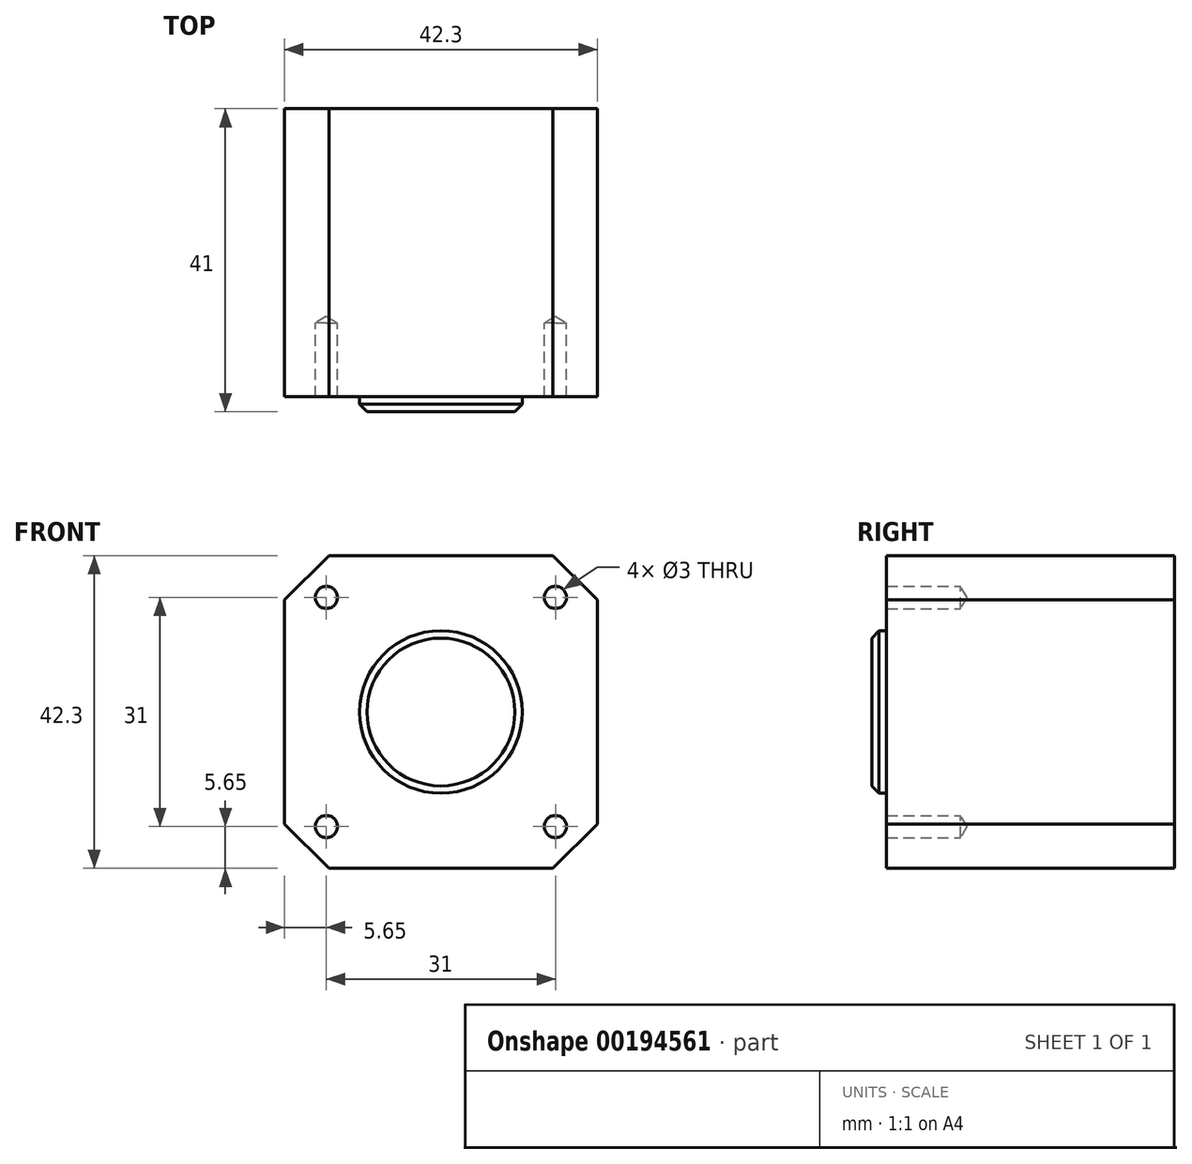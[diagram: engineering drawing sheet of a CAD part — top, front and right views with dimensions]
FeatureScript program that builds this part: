
annotation { "Feature Type Name" : "Feature", "Feature Type Description" : "" }
export const myFeature = defineFeature(function(context is Context, id is Id, definition is map)
    precondition{}
    {
        {
            var Q0;
            Q0=qCreatedBy(makeId("Front.planeOp"),FACE);
            var sketch = newSketch(context, id + "F0", { "sketchPlane" : qUnion([Q0])});
            skLineSegment(sketch, "E0.bottom", {"start": v(0, 0) * mm, "end": v(42.3, 0) * mm});
            skLineSegment(sketch, "E0.top", {"start": v(0, 42.3) * mm, "end": v(42.3, 42.3) * mm});
            skLineSegment(sketch, "E0.left", {"start": v(0, 0) * mm, "end": v(0, 42.3) * mm});
            skLineSegment(sketch, "E0.right", {"start": v(42.3, 0) * mm, "end": v(42.3, 42.3) * mm});
            skSolve(sketch);
        }
        {
            var Q0;
            Q0=makeQuery(id+"F0.imprint","IMPRINT",FACE,{"disambiguationData":[TD([[makeQuery(id+"F0.imprint","IMPRINT",EDGE,{"derivedFrom":sQuery(id+"F0.wireOp",EDGE,"E0.bottom")}),1.0]])]});
            extrude(context, id + "F1", {"entities" : qUnion([Q0]), "depth" : 39 * mm});
        }
        {
            var Q0;
            Q0=makeQuery(id+"F1.opExtrude","CAP_FACE",FACE,{"disambiguationData":[OSD([sQuery(id+"F0.wireOp",EDGE,"E0.bottom"),sQuery(id+"F0.wireOp",EDGE,"E0.top"),sQuery(id+"F0.wireOp",EDGE,"E0.left"),sQuery(id+"F0.wireOp",EDGE,"E0.right")])],"isStart":false});
            var sketch = newSketch(context, id + "F2", { "sketchPlane" : qUnion([Q0])});
            skCircle(sketch, "E1", {"center": v(21.15, 21.15) * mm, "radius": 11 * mm});
            skPoint(sketch, "E1.centerSnap0", {"position": v(42.3, 21.15) * mm});
            skPoint(sketch, "E1.centerSnap1", {"position": v(21.15, 42.3) * mm});
            skSolve(sketch);
        }
        {
            var Q0;
            Q0 = qSketchRegion(id + "F2", true);
            extrude(context, id + "F3", {"entities" : qUnion([Q0]), "operationType" : NewBodyOperationType.ADD, "depth" : 2 * mm});
        }
        {
            var Q0;
            Q0=makeQuery(id+"F3.opExtrude","CAP_EDGE",EDGE,{"disambiguationData":[OSD([sQuery(id+"F2.wireOp",EDGE,"E1")])],"isStart":false});
            chamfer(context, id + "F4", {"entities" : qUnion([Q0]), "width" : 1 * mm, "tangentPropagation" : true});
        }
        {
            var Q0;
            Q0=makeQuery(id+"F1.opExtrude","CAP_FACE",FACE,{"disambiguationData":[OSD([sQuery(id+"F0.wireOp",EDGE,"E0.bottom"),sQuery(id+"F0.wireOp",EDGE,"E0.top"),sQuery(id+"F0.wireOp",EDGE,"E0.left"),sQuery(id+"F0.wireOp",EDGE,"E0.right")])],"isStart":false});
            var sketch = newSketch(context, id + "F5", { "sketchPlane" : qUnion([Q0])});
            skLineSegment(sketch, "E2", {"start": v(21.15, 42.3) * mm, "end": v(21.15, 0) * mm, "construction": true});
            skLineSegment(sketch, "E3", {"start": v(42.3, 21.15) * mm, "end": v(0, 21.15) * mm, "construction": true});
            skPoint(sketch, "E4", {"position": v(5.65, 36.65) * mm});
            skPoint(sketch, "E5", {"position": v(36.65, 36.65) * mm});
            skPoint(sketch, "E6", {"position": v(36.65, 5.65) * mm});
            skPoint(sketch, "E7", {"position": v(5.65, 5.65) * mm});
            skSolve(sketch);
        }
        {
            var Q0;
            Q0=sQuery(id+"F5.wireOp",VERTEX,"E4");
            var Q1;
            Q1=sQuery(id+"F5.wireOp",VERTEX,"E5");
            var Q2;
            Q2=sQuery(id+"F5.wireOp",VERTEX,"E6");
            var Q3;
            Q3=sQuery(id+"F5.wireOp",VERTEX,"E7");
            var Q4;
            Q4=makeQuery(id+"F1.opExtrude","SWEPT_BODY",BODY,{"disambiguationData":[OSD([sQuery(id+"F0.wireOp",EDGE,"E0.bottom"),sQuery(id+"F0.wireOp",EDGE,"E0.top"),sQuery(id+"F0.wireOp",EDGE,"E0.left"),sQuery(id+"F0.wireOp",EDGE,"E0.right")])]});
            hole(context, id + "F6", {"style" : HoleStyle.SIMPLE, "endStyle" : HoleEndStyle.BLIND, "holeDiameter" : 3 * mm, "holeDepth" : 10 * mm, "locations" : qUnion([Q0, Q1, Q2, Q3]), "scope" : qUnion([Q4]), "startStyle" : HoleStartStyle.SKETCH});
        }
        {
            var Q0;
            Q0=makeQuery(id+"F1.opExtrude","SWEPT_EDGE",EDGE,{"disambiguationData":[OSD([sQuery(id+"F0.wireOp",EDGE,"E0.top"),sQuery(id+"F0.wireOp",EDGE,"E0.left")])]});
            var Q1;
            Q1=makeQuery(id+"F1.opExtrude","SWEPT_EDGE",EDGE,{"disambiguationData":[OSD([sQuery(id+"F0.wireOp",EDGE,"E0.bottom"),sQuery(id+"F0.wireOp",EDGE,"E0.left")])]});
            var Q2;
            Q2=makeQuery(id+"F1.opExtrude","SWEPT_EDGE",EDGE,{"disambiguationData":[OSD([sQuery(id+"F0.wireOp",EDGE,"E0.top"),sQuery(id+"F0.wireOp",EDGE,"E0.right")])]});
            var Q3;
            Q3=makeQuery(id+"F1.opExtrude","SWEPT_EDGE",EDGE,{"disambiguationData":[OSD([sQuery(id+"F0.wireOp",EDGE,"E0.bottom"),sQuery(id+"F0.wireOp",EDGE,"E0.right")])]});
            chamfer(context, id + "F7", {"entities" : qUnion([Q0, Q1, Q2, Q3]), "width" : 6 * mm, "tangentPropagation" : true});
        }
    });
